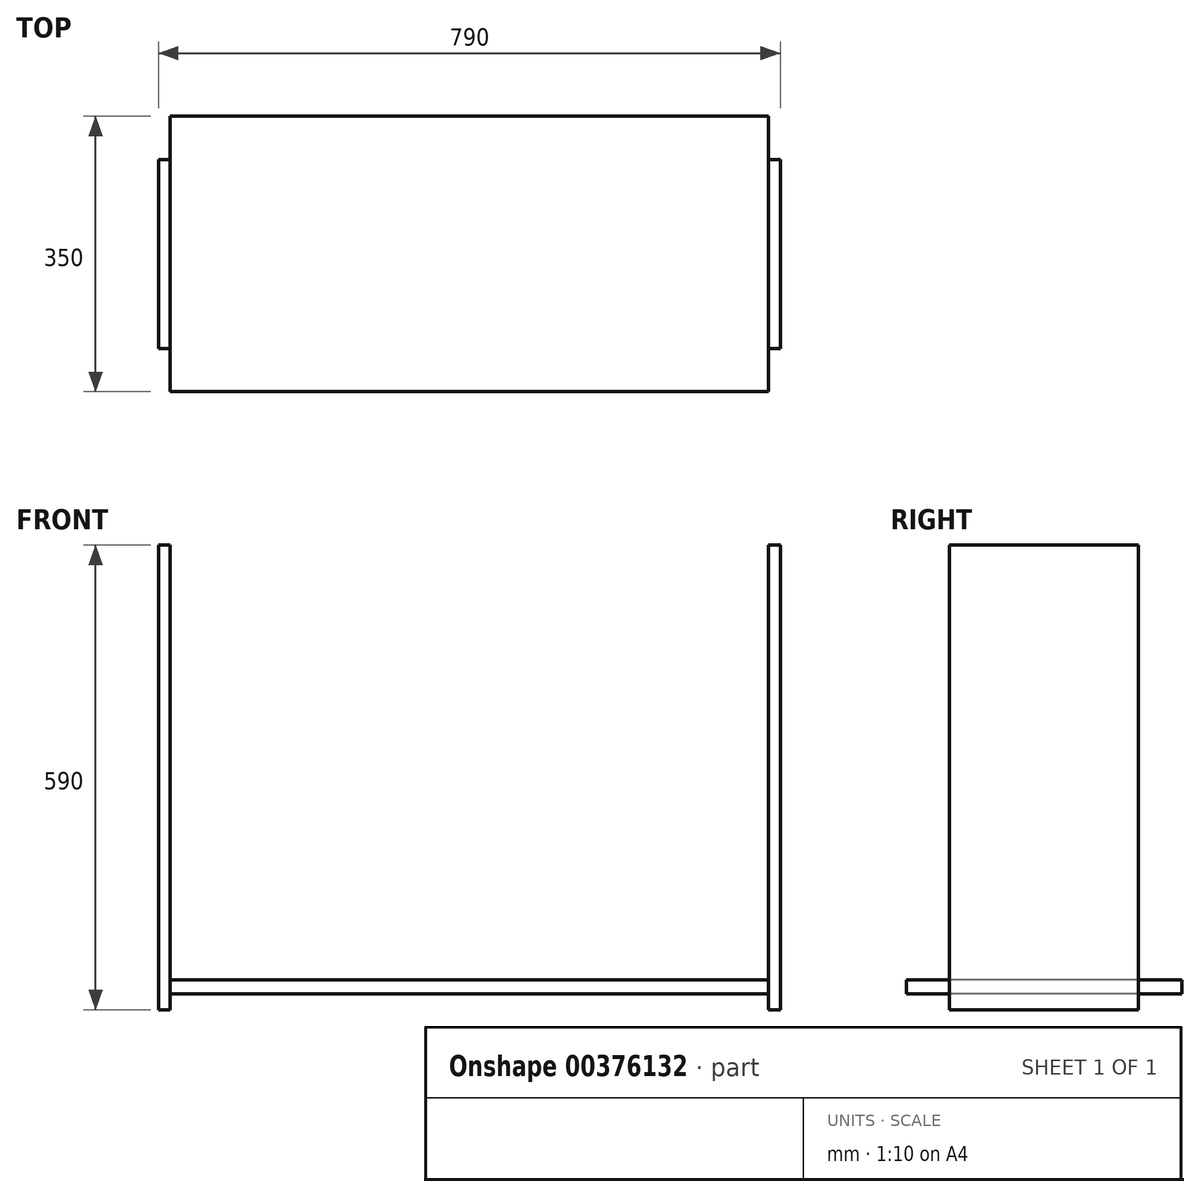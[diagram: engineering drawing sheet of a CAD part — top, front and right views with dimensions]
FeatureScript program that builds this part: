
annotation { "Feature Type Name" : "Feature", "Feature Type Description" : "" }
export const myFeature = defineFeature(function(context is Context, id is Id, definition is map)
    precondition{}
    {
        {
            var Q0;
            Q0=qCreatedBy(makeId("Top.planeOp"),FACE);
            var sketch = newSketch(context, id + "F0", { "sketchPlane" : qUnion([Q0])});
            skLineSegment(sketch, "E0.bottom", {"start": v(-380, 175) * mm, "end": v(380, 175) * mm});
            skLineSegment(sketch, "E0.top", {"start": v(-380, -175) * mm, "end": v(380, -175) * mm});
            skLineSegment(sketch, "E0.left", {"start": v(-380, 175) * mm, "end": v(-380, -175) * mm});
            skLineSegment(sketch, "E0.right", {"start": v(380, 175) * mm, "end": v(380, -175) * mm});
            skPoint(sketch, "E1", {"position": v(0, 175) * mm});
            skPoint(sketch, "E2", {"position": v(-380, 0) * mm});
            skSolve(sketch);
        }
        {
            var Q0;
            Q0=makeQuery(id+"F0.imprint","IMPRINT",FACE,{"disambiguationData":[TD([[makeQuery(id+"F0.imprint","IMPRINT",EDGE,{"derivedFrom":sQuery(id+"F0.wireOp",EDGE,"E0.bottom")}),-1.0]])]});
            extrude(context, id + "F1", {"entities" : qUnion([Q0]), "depth" : 18 * mm});
        }
        {
            var Q0;
            Q0=makeQuery(id+"F1.opExtrude","SWEPT_FACE",FACE,{"disambiguationData":[OSD([sQuery(id+"F0.wireOp",EDGE,"E0.left")])]});
            var sketch = newSketch(context, id + "F2", { "sketchPlane" : qUnion([Q0])});
            skLineSegment(sketch, "E3.bottom", {"start": v(120.42, -20) * mm, "end": v(-119.58, -20) * mm});
            skLineSegment(sketch, "E3.top", {"start": v(120.42, 570) * mm, "end": v(-119.58, 570) * mm});
            skLineSegment(sketch, "E3.left", {"start": v(120.42, -20) * mm, "end": v(120.42, 570) * mm});
            skLineSegment(sketch, "E3.right", {"start": v(-119.58, -20) * mm, "end": v(-119.58, 570) * mm});
            skSolve(sketch);
        }
        {
            var Q0;
            {var subQ0=sQuery(id+"F2.wireOp",EDGE,"E3.bottom");Q0=makeQuery(id+"F2.imprint","IMPRINT",FACE,{"disambiguationData":[TD([[makeQuery(id+"F2.imprint","IMPRINT",EDGE,{"derivedFrom":subQ0}),-1.0]])]});}
            var Q1;
            {var subQ0=sQuery(id+"F2.wireOp",EDGE,"E3.left");var subQ1=sQuery(id+"F0.wireOp",EDGE,"E0.left");var subQ2=makeQuery(id+"F1.opExtrude","CAP_EDGE",EDGE,{"disambiguationData":[OSD([subQ1])],"isStart":true});var subQ3=makeQuery(id+"F2.imprint","INTERSECT",VERTEX,{"derivedFrom":[subQ2,subQ0]});Q1=makeQuery(id+"F2.imprint","IMPRINT",FACE,{"disambiguationData":[TD([[makeQuery(id+"F2.imprint","IMPRINT",EDGE,{"disambiguationData":[TD([[subQ3,-1.0]])],"derivedFrom":subQ0}),1.0]])]});}
            var Q2;
            {var subQ0=sQuery(id+"F2.wireOp",EDGE,"E3.top");Q2=makeQuery(id+"F2.imprint","IMPRINT",FACE,{"disambiguationData":[TD([[makeQuery(id+"F2.imprint","IMPRINT",EDGE,{"derivedFrom":subQ0}),1.0]])]});}
            extrude(context, id + "F3", {"entities" : qUnion([Q0, Q1, Q2]), "depth" : 15 * mm});
        }
        {
            var Q0;
            Q0=makeQuery(id+"F1.opExtrude","SWEPT_FACE",FACE,{"disambiguationData":[OSD([sQuery(id+"F0.wireOp",EDGE,"E0.right")])]});
            var sketch = newSketch(context, id + "F4", { "sketchPlane" : qUnion([Q0])});
            skLineSegment(sketch, "E4.bottom", {"start": v(119.58, -20) * mm, "end": v(-120.42, -20) * mm});
            skLineSegment(sketch, "E4.top", {"start": v(119.58, 570) * mm, "end": v(-120.42, 570) * mm});
            skLineSegment(sketch, "E4.left", {"start": v(119.58, -20) * mm, "end": v(119.58, 570) * mm});
            skLineSegment(sketch, "E4.right", {"start": v(-120.42, -20) * mm, "end": v(-120.42, 570) * mm});
            skSolve(sketch);
        }
        {
            var Q0;
            {var subQ0=sQuery(id+"F4.wireOp",EDGE,"E4.top");Q0=makeQuery(id+"F4.imprint","IMPRINT",FACE,{"disambiguationData":[TD([[makeQuery(id+"F4.imprint","IMPRINT",EDGE,{"derivedFrom":subQ0}),1.0]])]});}
            var Q1;
            {var subQ0=sQuery(id+"F4.wireOp",EDGE,"E4.left");var subQ1=sQuery(id+"F0.wireOp",EDGE,"E0.right");var subQ2=makeQuery(id+"F1.opExtrude","CAP_EDGE",EDGE,{"disambiguationData":[OSD([subQ1])],"isStart":true});var subQ3=makeQuery(id+"F4.imprint","INTERSECT",VERTEX,{"derivedFrom":[subQ2,subQ0]});Q1=makeQuery(id+"F4.imprint","IMPRINT",FACE,{"disambiguationData":[TD([[makeQuery(id+"F4.imprint","IMPRINT",EDGE,{"disambiguationData":[TD([[subQ3,-1.0]])],"derivedFrom":subQ0}),1.0]])]});}
            var Q2;
            {var subQ0=sQuery(id+"F4.wireOp",EDGE,"E4.bottom");Q2=makeQuery(id+"F4.imprint","IMPRINT",FACE,{"disambiguationData":[TD([[makeQuery(id+"F4.imprint","IMPRINT",EDGE,{"derivedFrom":subQ0}),-1.0]])]});}
            extrude(context, id + "F5", {"entities" : qUnion([Q0, Q1, Q2]), "operationType" : NewBodyOperationType.ADD, "depth" : 15 * mm});
        }
    });
